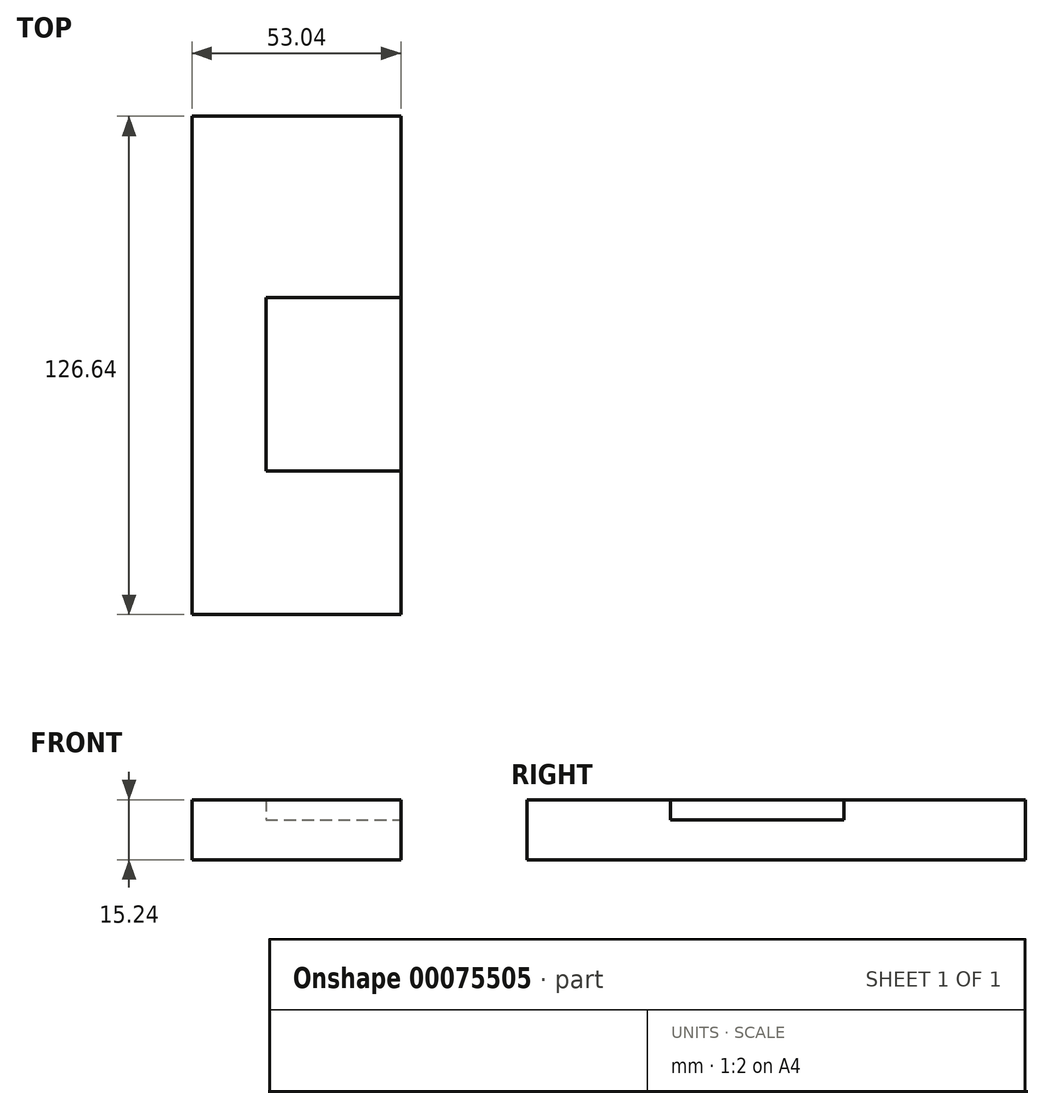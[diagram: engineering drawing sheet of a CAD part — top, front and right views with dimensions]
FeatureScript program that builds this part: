
annotation { "Feature Type Name" : "Feature", "Feature Type Description" : "" }
export const myFeature = defineFeature(function(context is Context, id is Id, definition is map)
    precondition{}
    {
        {
            var Q0;
            Q0=qCreatedBy(makeId("Top.planeOp"),FACE);
            var sketch = newSketch(context, id + "F0", { "sketchPlane" : qUnion([Q0])});
            skLineSegment(sketch, "E0.bottom", {"start": v(-22.35, 56.17) * mm, "end": v(30.7, 56.17) * mm});
            skLineSegment(sketch, "E0.top", {"start": v(-22.35, -70.47) * mm, "end": v(30.7, -70.47) * mm});
            skLineSegment(sketch, "E0.left", {"start": v(-22.35, 56.17) * mm, "end": v(-22.35, -70.47) * mm});
            skLineSegment(sketch, "E0.right", {"start": v(30.7, 56.17) * mm, "end": v(30.7, -70.47) * mm});
            skSolve(sketch);
        }
        {
            var Q0;
            Q0 = qSketchRegion(id + "F0", true);
            extrude(context, id + "F1", {"entities" : qUnion([Q0]), "depth" : 10.16 * mm});
        }
        {
            var Q0;
            Q0=makeQuery(id+"F1.opExtrude","CAP_FACE",FACE,{"disambiguationData":[OSD([sQuery(id+"F0.wireOp",EDGE,"E0.bottom"),sQuery(id+"F0.wireOp",EDGE,"E0.top"),sQuery(id+"F0.wireOp",EDGE,"E0.left"),sQuery(id+"F0.wireOp",EDGE,"E0.right")])],"isStart":false});
            var sketch = newSketch(context, id + "F2", { "sketchPlane" : qUnion([Q0])});
            skLineSegment(sketch, "E1.bottom", {"start": v(-22.35, -70.47) * mm, "end": v(-3.6, -70.47) * mm});
            skLineSegment(sketch, "E1.top", {"start": v(-22.35, 56.17) * mm, "end": v(-3.6, 56.17) * mm});
            skLineSegment(sketch, "E1.left", {"start": v(-22.35, -70.47) * mm, "end": v(-22.35, 56.17) * mm});
            skLineSegment(sketch, "E1.right", {"start": v(-3.6, -70.47) * mm, "end": v(-3.6, 56.17) * mm});
            skLineSegment(sketch, "E2.bottom", {"start": v(-3.6, -70.47) * mm, "end": v(30.7, -70.47) * mm});
            skLineSegment(sketch, "E2.top", {"start": v(-3.6, -33.94) * mm, "end": v(30.7, -33.94) * mm});
            skLineSegment(sketch, "E2.left", {"start": v(-3.6, -70.47) * mm, "end": v(-3.6, -33.94) * mm});
            skLineSegment(sketch, "E2.right", {"start": v(30.7, -70.47) * mm, "end": v(30.7, -33.94) * mm});
            skLineSegment(sketch, "E3.bottom", {"start": v(-3.6, 10.05) * mm, "end": v(30.7, 10.05) * mm});
            skLineSegment(sketch, "E3.top", {"start": v(-3.6, 56.17) * mm, "end": v(30.7, 56.17) * mm});
            skLineSegment(sketch, "E3.left", {"start": v(-3.6, 10.05) * mm, "end": v(-3.6, 56.17) * mm});
            skLineSegment(sketch, "E3.right", {"start": v(30.7, 10.05) * mm, "end": v(30.7, 56.17) * mm});
            skSolve(sketch);
        }
        {
            var Q0;
            Q0=makeQuery(id+"F2.imprint","IMPRINT",FACE,{"disambiguationData":[TD([[makeQuery(id+"F2.imprint","IMPRINT",EDGE,{"derivedFrom":sQuery(id+"F2.wireOp",EDGE,"E2.bottom")}),1.0]])]});
            var Q1;
            Q1=makeQuery(id+"F2.imprint","IMPRINT",FACE,{"disambiguationData":[TD([[makeQuery(id+"F2.imprint","IMPRINT",EDGE,{"derivedFrom":sQuery(id+"F2.wireOp",EDGE,"E1.bottom")}),1.0]])]});
            var Q2;
            Q2=makeQuery(id+"F2.imprint","IMPRINT",FACE,{"disambiguationData":[TD([[makeQuery(id+"F2.imprint","IMPRINT",EDGE,{"derivedFrom":sQuery(id+"F2.wireOp",EDGE,"E3.bottom")}),1.0]])]});
            extrude(context, id + "F3", {"entities" : qUnion([Q0, Q1, Q2]), "operationType" : NewBodyOperationType.ADD, "depth" : 5.08 * mm});
        }
    });
